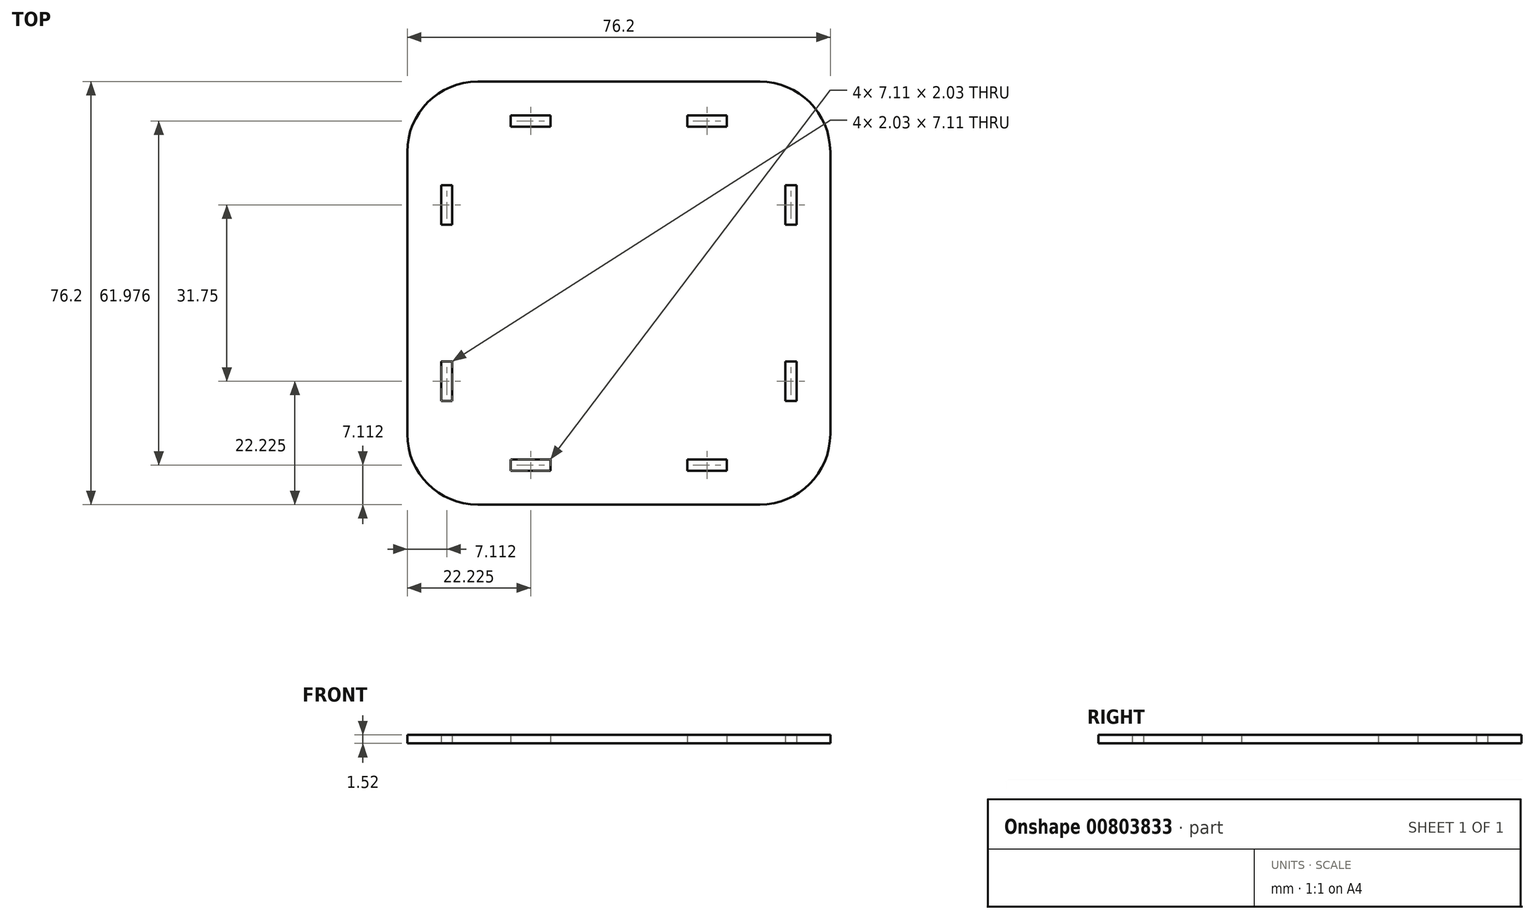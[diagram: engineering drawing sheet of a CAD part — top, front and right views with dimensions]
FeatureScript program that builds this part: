
annotation { "Feature Type Name" : "Feature", "Feature Type Description" : "" }
export const myFeature = defineFeature(function(context is Context, id is Id, definition is map)
    precondition{}
    {
        {
            var Q0;
            Q0=qCreatedBy(makeId("Top.planeOp"),FACE);
            var sketch = newSketch(context, id + "F0", { "sketchPlane" : qUnion([Q0])});
            skLineSegment(sketch, "E0.bottom", {"start": v(38.1, 38.1) * mm, "end": v(-38.1, 38.1) * mm});
            skLineSegment(sketch, "E0.top", {"start": v(38.1, -38.1) * mm, "end": v(-38.1, -38.1) * mm});
            skLineSegment(sketch, "E0.left", {"start": v(38.1, 38.1) * mm, "end": v(38.1, -38.1) * mm});
            skLineSegment(sketch, "E0.right", {"start": v(-38.1, 38.1) * mm, "end": v(-38.1, -38.1) * mm});
            skPoint(sketch, "E0.middle", {"position": v(0, 0) * mm});
            skLineSegment(sketch, "E1.bottom", {"start": v(31.75, 31.75) * mm, "end": v(-31.75, 31.75) * mm, "construction": true});
            skLineSegment(sketch, "E1.top", {"start": v(31.75, -31.75) * mm, "end": v(-31.75, -31.75) * mm, "construction": true});
            skLineSegment(sketch, "E1.left", {"start": v(31.75, 31.75) * mm, "end": v(31.75, -31.75) * mm, "construction": true});
            skLineSegment(sketch, "E1.right", {"start": v(-31.75, 31.75) * mm, "end": v(-31.75, -31.75) * mm, "construction": true});
            skLineSegment(sketch, "E2.bottom", {"start": v(-19.18, -31.75) * mm, "end": v(-12.57, -31.75) * mm});
            skLineSegment(sketch, "E2.top", {"start": v(-19.18, -30.23) * mm, "end": v(-12.57, -30.23) * mm});
            skLineSegment(sketch, "E2.left", {"start": v(-19.18, -31.75) * mm, "end": v(-19.18, -30.23) * mm});
            skLineSegment(sketch, "E2.right", {"start": v(-12.57, -31.75) * mm, "end": v(-12.57, -30.23) * mm});
            skPoint(sketch, "E3", {"position": v(-15.88, -31.75) * mm});
            skLineSegment(sketch, "E4.0", {"start": v(-19.43, -29.97) * mm, "end": v(-12.32, -29.97) * mm});
            skLineSegment(sketch, "E4.1", {"start": v(-19.43, -32) * mm, "end": v(-19.43, -29.97) * mm});
            skLineSegment(sketch, "E4.2", {"start": v(-19.43, -32) * mm, "end": v(-12.32, -32) * mm});
            skLineSegment(sketch, "E4.3", {"start": v(-12.32, -32) * mm, "end": v(-12.32, -29.97) * mm});
            skLineSegment(sketch, "E5.MirrorCS", {"start": v(19.43, -29.97) * mm, "end": v(12.32, -29.97) * mm});
            skLineSegment(sketch, "E6.MirrorCS", {"start": v(19.43, -32) * mm, "end": v(19.43, -29.97) * mm});
            skLineSegment(sketch, "E7.MirrorCS", {"start": v(19.43, -32) * mm, "end": v(12.32, -32) * mm});
            skLineSegment(sketch, "E8.MirrorCS", {"start": v(12.32, -32) * mm, "end": v(12.32, -29.97) * mm});
            skLineSegment(sketch, "E9.MirrorCS", {"start": v(-19.43, 32) * mm, "end": v(-19.43, 29.97) * mm});
            skLineSegment(sketch, "E10.MirrorCS", {"start": v(-19.43, 29.97) * mm, "end": v(-12.32, 29.97) * mm});
            skLineSegment(sketch, "E11.MirrorCS", {"start": v(-12.32, 32) * mm, "end": v(-12.32, 29.97) * mm});
            skLineSegment(sketch, "E12.MirrorCS", {"start": v(-19.43, 32) * mm, "end": v(-12.32, 32) * mm});
            skLineSegment(sketch, "E13.MirrorCS", {"start": v(19.43, 29.97) * mm, "end": v(12.32, 29.97) * mm});
            skLineSegment(sketch, "E14.MirrorCS", {"start": v(19.43, 32) * mm, "end": v(19.43, 29.97) * mm});
            skLineSegment(sketch, "E15.MirrorCS", {"start": v(19.43, 32) * mm, "end": v(12.32, 32) * mm});
            skLineSegment(sketch, "E16.MirrorCS", {"start": v(12.32, 32) * mm, "end": v(12.32, 29.97) * mm});
            skLineSegment(sketch, "E17.bottom", {"start": v(-31.75, -19.18) * mm, "end": v(-30.23, -19.18) * mm});
            skLineSegment(sketch, "E17.top", {"start": v(-31.75, -12.57) * mm, "end": v(-30.23, -12.57) * mm});
            skLineSegment(sketch, "E17.left", {"start": v(-31.75, -19.18) * mm, "end": v(-31.75, -12.57) * mm});
            skLineSegment(sketch, "E17.right", {"start": v(-30.23, -19.18) * mm, "end": v(-30.23, -12.57) * mm});
            skPoint(sketch, "E18", {"position": v(-31.75, -15.88) * mm});
            skLineSegment(sketch, "E19.0", {"start": v(-29.97, -19.43) * mm, "end": v(-29.97, -12.32) * mm});
            skLineSegment(sketch, "E19.1", {"start": v(-32, -19.43) * mm, "end": v(-29.97, -19.43) * mm});
            skLineSegment(sketch, "E19.2", {"start": v(-32, -19.43) * mm, "end": v(-32, -12.32) * mm});
            skLineSegment(sketch, "E19.3", {"start": v(-32, -12.32) * mm, "end": v(-29.97, -12.32) * mm});
            skLineSegment(sketch, "E20.MirrorCS", {"start": v(-32, 19.43) * mm, "end": v(-32, 12.32) * mm});
            skLineSegment(sketch, "E21.MirrorCS", {"start": v(-32, 12.32) * mm, "end": v(-29.97, 12.32) * mm});
            skLineSegment(sketch, "E22.MirrorCS", {"start": v(-29.97, 19.43) * mm, "end": v(-29.97, 12.32) * mm});
            skLineSegment(sketch, "E23.MirrorCS", {"start": v(-32, 19.43) * mm, "end": v(-29.97, 19.43) * mm});
            skLineSegment(sketch, "E24.MirrorCS", {"start": v(32, -19.43) * mm, "end": v(32, -12.32) * mm});
            skLineSegment(sketch, "E25.MirrorCS", {"start": v(32, -12.32) * mm, "end": v(29.97, -12.32) * mm});
            skLineSegment(sketch, "E26.MirrorCS", {"start": v(29.97, -19.43) * mm, "end": v(29.97, -12.32) * mm});
            skLineSegment(sketch, "E27.MirrorCS", {"start": v(32, -19.43) * mm, "end": v(29.97, -19.43) * mm});
            skLineSegment(sketch, "E28.MirrorCS", {"start": v(29.97, 19.43) * mm, "end": v(29.97, 12.32) * mm});
            skLineSegment(sketch, "E29.MirrorCS", {"start": v(32, 12.32) * mm, "end": v(29.97, 12.32) * mm});
            skLineSegment(sketch, "E30.MirrorCS", {"start": v(32, 19.43) * mm, "end": v(32, 12.32) * mm});
            skLineSegment(sketch, "E31.MirrorCS", {"start": v(32, 19.43) * mm, "end": v(29.97, 19.43) * mm});
            skSolve(sketch);
        }
        {
            var Q0;
            Q0=makeQuery(id+"F0.imprint","IMPRINT",FACE,{"disambiguationData":[TD([[makeQuery(id+"F0.imprint","IMPRINT",EDGE,{"derivedFrom":sQuery(id+"F0.wireOp",EDGE,"E0.bottom")}),1.0]])]});
            extrude(context, id + "F1", {"entities" : qUnion([Q0]), "depth" : 1.52 * mm, "offsetDistance" : 25.4 * mm});
        }
        {
            var Q0;
            Q0=makeQuery(id+"F1.opExtrude","SWEPT_EDGE",EDGE,{"disambiguationData":[OSD([sQuery(id+"F0.wireOp",EDGE,"E0.bottom"),sQuery(id+"F0.wireOp",EDGE,"E0.right")])]});
            var Q1;
            Q1=makeQuery(id+"F1.opExtrude","SWEPT_EDGE",EDGE,{"disambiguationData":[OSD([sQuery(id+"F0.wireOp",EDGE,"E0.bottom"),sQuery(id+"F0.wireOp",EDGE,"E0.left")])]});
            var Q2;
            Q2=makeQuery(id+"F1.opExtrude","SWEPT_EDGE",EDGE,{"disambiguationData":[OSD([sQuery(id+"F0.wireOp",EDGE,"E0.top"),sQuery(id+"F0.wireOp",EDGE,"E0.left")])]});
            var Q3;
            Q3=makeQuery(id+"F1.opExtrude","SWEPT_EDGE",EDGE,{"disambiguationData":[OSD([sQuery(id+"F0.wireOp",EDGE,"E0.top"),sQuery(id+"F0.wireOp",EDGE,"E0.right")])]});
            fillet(context, id + "F2", {"entities" : qUnion([Q0, Q1, Q2, Q3]), "radius" : 12.7 * mm, "tangentPropagation" : true, "allowEdgeOverflow" : false});
        }
    });
